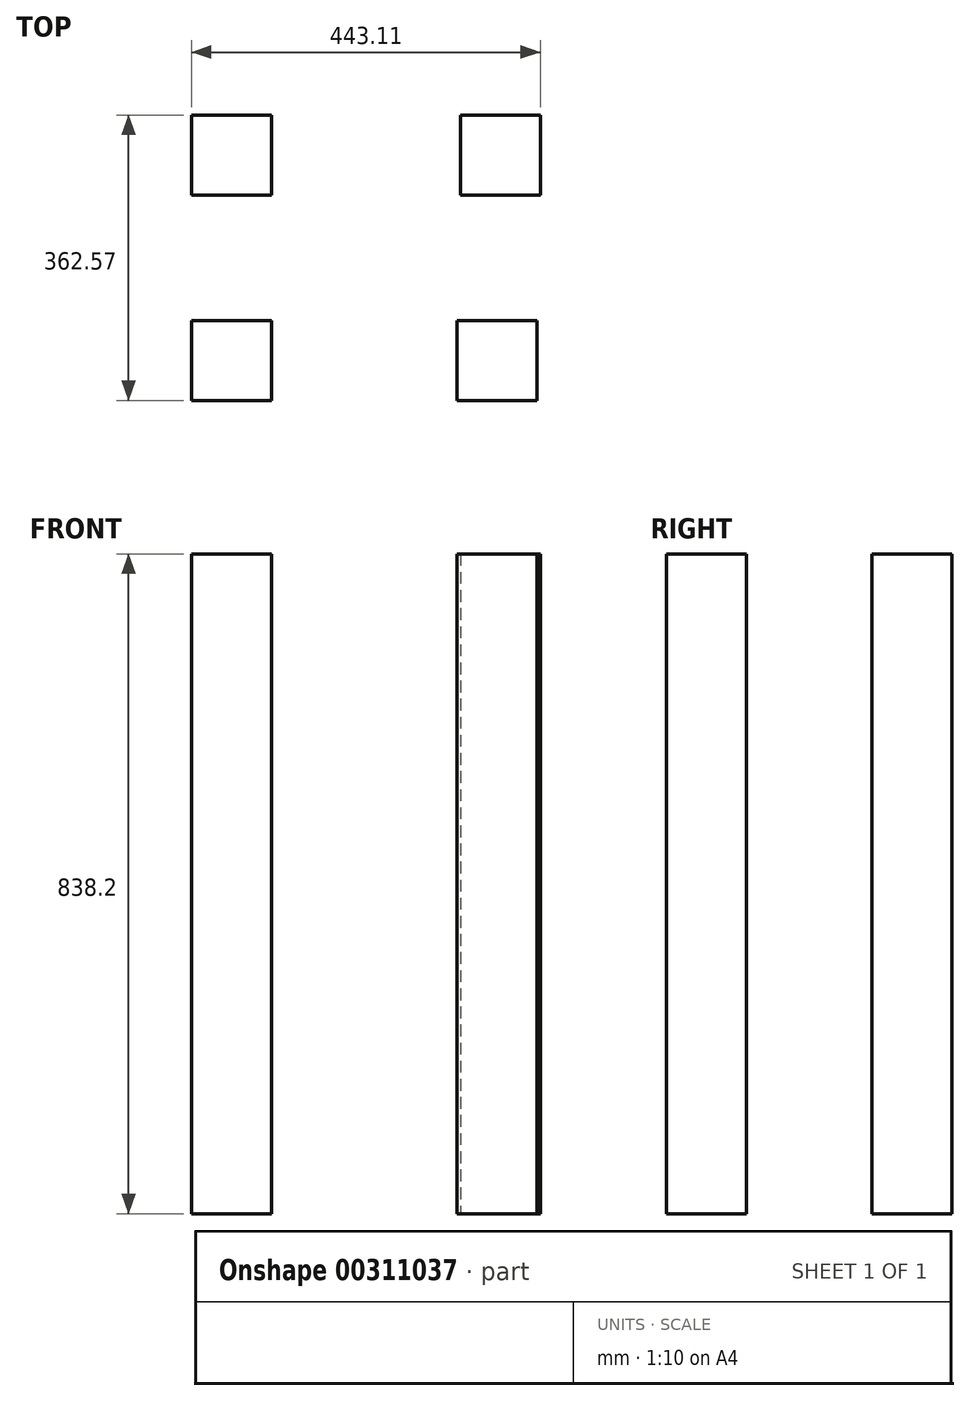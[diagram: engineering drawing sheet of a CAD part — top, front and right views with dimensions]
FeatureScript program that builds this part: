
annotation { "Feature Type Name" : "Feature", "Feature Type Description" : "" }
export const myFeature = defineFeature(function(context is Context, id is Id, definition is map)
    precondition{}
    {
        {
            var Q0;
            Q0=qCreatedBy(makeId("Top.planeOp"),FACE);
            var sketch = newSketch(context, id + "F0", { "sketchPlane" : qUnion([Q0])});
            skLineSegment(sketch, "E0.bottom", {"start": v(-181.6, 125.22) * mm, "end": v(-80, 125.22) * mm});
            skLineSegment(sketch, "E0.top", {"start": v(-181.6, 23.62) * mm, "end": v(-80, 23.62) * mm});
            skLineSegment(sketch, "E0.left", {"start": v(-181.6, 125.22) * mm, "end": v(-181.6, 23.62) * mm});
            skLineSegment(sketch, "E0.right", {"start": v(-80, 125.22) * mm, "end": v(-80, 23.62) * mm});
            skPoint(sketch, "E1.firstSnap0", {"position": v(-130.8, 125.22) * mm});
            skLineSegment(sketch, "E1.bottom", {"start": v(159.9, 125.22) * mm, "end": v(261.5, 125.22) * mm});
            skLineSegment(sketch, "E1.top", {"start": v(159.9, 23.62) * mm, "end": v(261.5, 23.62) * mm});
            skLineSegment(sketch, "E1.left", {"start": v(159.9, 125.22) * mm, "end": v(159.9, 23.62) * mm});
            skLineSegment(sketch, "E1.right", {"start": v(261.5, 125.22) * mm, "end": v(261.5, 23.62) * mm});
            skLineSegment(sketch, "E2.bottom", {"start": v(-181.6, -135.75) * mm, "end": v(-80, -135.75) * mm});
            skLineSegment(sketch, "E2.top", {"start": v(-181.6, -237.35) * mm, "end": v(-80, -237.35) * mm});
            skLineSegment(sketch, "E2.left", {"start": v(-181.6, -135.75) * mm, "end": v(-181.6, -237.35) * mm});
            skLineSegment(sketch, "E2.right", {"start": v(-80, -135.75) * mm, "end": v(-80, -237.35) * mm});
            skLineSegment(sketch, "E3.bottom", {"start": v(155.59, -135.75) * mm, "end": v(257.19, -135.75) * mm});
            skLineSegment(sketch, "E3.top", {"start": v(155.59, -237.35) * mm, "end": v(257.19, -237.35) * mm});
            skLineSegment(sketch, "E3.left", {"start": v(155.59, -135.75) * mm, "end": v(155.59, -237.35) * mm});
            skLineSegment(sketch, "E3.right", {"start": v(257.19, -135.75) * mm, "end": v(257.19, -237.35) * mm});
            skSolve(sketch);
        }
        {
            var Q0;
            Q0=makeQuery(id+"F0.imprint","IMPRINT",FACE,{"disambiguationData":[TD([[makeQuery(id+"F0.imprint","IMPRINT",EDGE,{"derivedFrom":sQuery(id+"F0.wireOp",EDGE,"E0.bottom")}),-1.0]])]});
            var Q1;
            Q1=makeQuery(id+"F0.imprint","IMPRINT",FACE,{"disambiguationData":[TD([[makeQuery(id+"F0.imprint","IMPRINT",EDGE,{"derivedFrom":sQuery(id+"F0.wireOp",EDGE,"E3.bottom")}),-1.0]])]});
            var Q2;
            Q2=makeQuery(id+"F0.imprint","IMPRINT",FACE,{"disambiguationData":[TD([[makeQuery(id+"F0.imprint","IMPRINT",EDGE,{"derivedFrom":sQuery(id+"F0.wireOp",EDGE,"E2.bottom")}),-1.0]])]});
            var Q3;
            Q3=makeQuery(id+"F0.imprint","IMPRINT",FACE,{"disambiguationData":[TD([[makeQuery(id+"F0.imprint","IMPRINT",EDGE,{"derivedFrom":sQuery(id+"F0.wireOp",EDGE,"E1.bottom")}),-1.0]])]});
            extrude(context, id + "F1", {"entities" : qUnion([Q0, Q1, Q2, Q3]), "depth" : 838.2 * mm});
        }
    });
